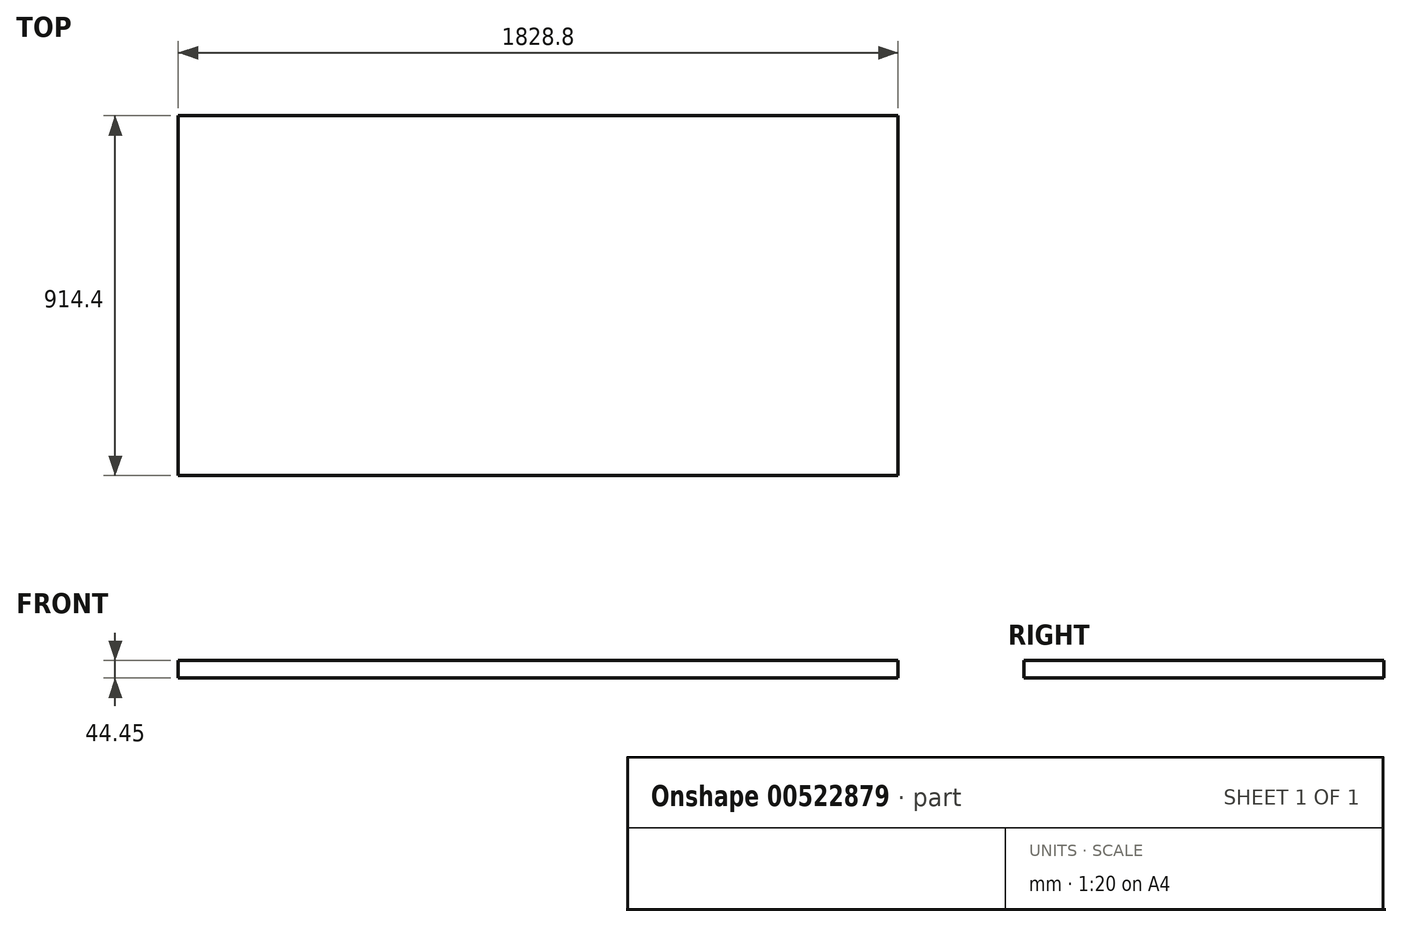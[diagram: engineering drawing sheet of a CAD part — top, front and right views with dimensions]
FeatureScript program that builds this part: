
annotation { "Feature Type Name" : "Feature", "Feature Type Description" : "" }
export const myFeature = defineFeature(function(context is Context, id is Id, definition is map)
    precondition{}
    {
        {
            var Q0;
            Q0=qCreatedBy(makeId("Top.planeOp"),FACE);
            var sketch = newSketch(context, id + "F0", { "sketchPlane" : qUnion([Q0])});
            skLineSegment(sketch, "E0.bottom", {"start": v(-914.4, 457.2) * mm, "end": v(914.4, 457.2) * mm});
            skLineSegment(sketch, "E0.top", {"start": v(-914.4, -457.2) * mm, "end": v(914.4, -457.2) * mm});
            skLineSegment(sketch, "E0.left", {"start": v(-914.4, 457.2) * mm, "end": v(-914.4, -457.2) * mm});
            skLineSegment(sketch, "E0.right", {"start": v(914.4, 457.2) * mm, "end": v(914.4, -457.2) * mm});
            skPoint(sketch, "E0.middle", {"position": v(0, 0) * mm});
            skSolve(sketch);
        }
        {
            var Q0;
            Q0 = qSketchRegion(id + "F0", true);
            extrude(context, id + "F1", {"entities" : qUnion([Q0]), "depth" : 44.45 * mm, "offsetDistance" : 25 * mm});
        }
    });
